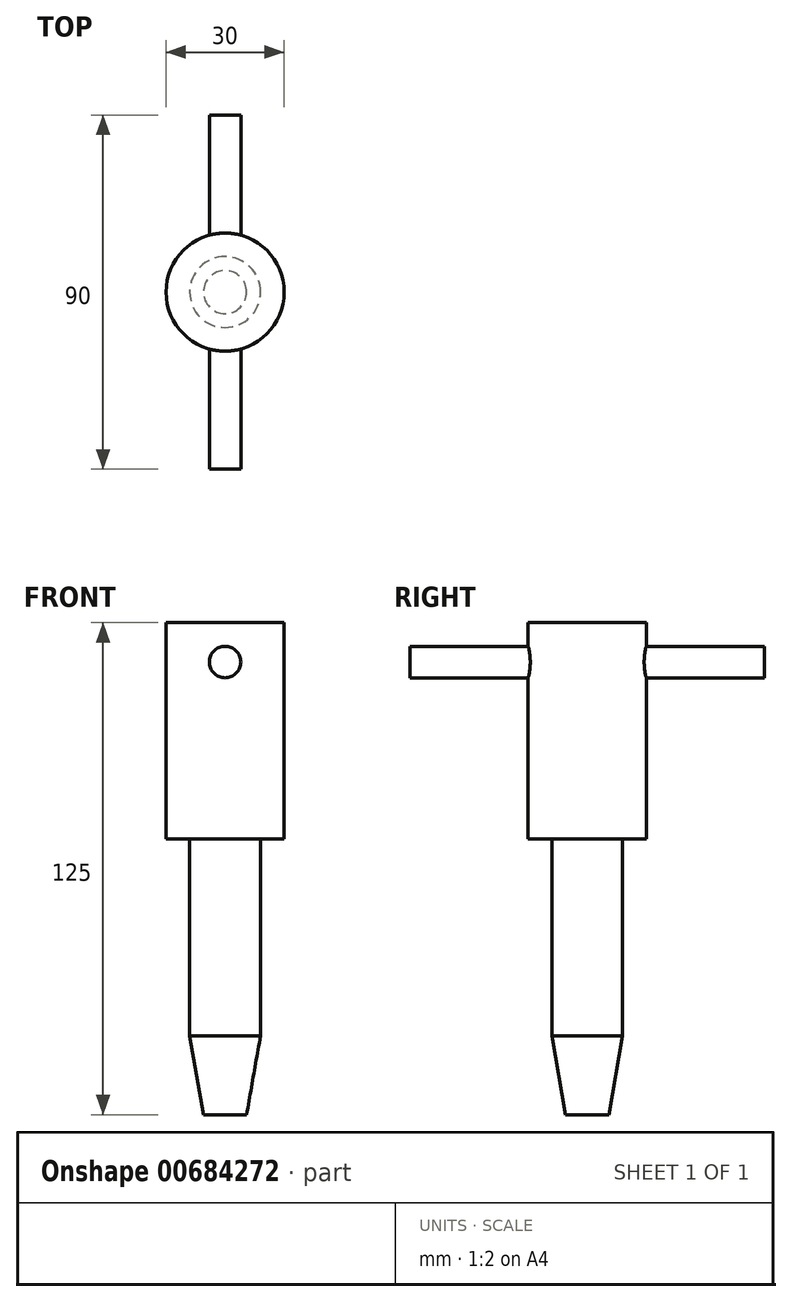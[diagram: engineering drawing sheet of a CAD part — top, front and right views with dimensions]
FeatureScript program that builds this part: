
annotation { "Feature Type Name" : "Feature", "Feature Type Description" : "" }
export const myFeature = defineFeature(function(context is Context, id is Id, definition is map)
    precondition{}
    {
        {
            var Q0;
            Q0=qCreatedBy(makeId("Front.planeOp"),FACE);
            var sketch = newSketch(context, id + "F0", { "sketchPlane" : qUnion([Q0])});
            skLineSegment(sketch, "E0", {"start": v(0, 0) * mm, "end": v(0, -70) * mm});
            skLineSegment(sketch, "E1", {"start": v(0, -70) * mm, "end": v(5.47, -70) * mm});
            skLineSegment(sketch, "E2", {"start": v(5.47, -70) * mm, "end": v(9, -50) * mm});
            skLineSegment(sketch, "E3", {"start": v(9, -50) * mm, "end": v(9, 0) * mm});
            skLineSegment(sketch, "E4", {"start": v(9, 0) * mm, "end": v(15, 0) * mm});
            skLineSegment(sketch, "E5", {"start": v(15, 0) * mm, "end": v(15, 55) * mm});
            skLineSegment(sketch, "E6", {"start": v(15, 55) * mm, "end": v(0, 55) * mm});
            skLineSegment(sketch, "E7", {"start": v(0, 55) * mm, "end": v(0, 0) * mm});
            skSolve(sketch);
        }
        {
            var Q0;
            Q0=makeQuery(id+"F0.imprint","IMPRINT",FACE,{"disambiguationData":[TD([[makeQuery(id+"F0.imprint","IMPRINT",EDGE,{"derivedFrom":sQuery(id+"F0.wireOp",EDGE,"E0")}),1.0]])]});
            var Q1;
            Q1=sQuery(id+"F0.wireOp",EDGE,"E7");
            revolve(context, id + "F1", {"entities" : qUnion([Q0]), "axis" : qUnion([Q1]), "revolveType" : RevolveType.FULL});
        }
        {
            var Q0;
            Q0=qCreatedBy(makeId("Front.planeOp"),FACE);
            var sketch = newSketch(context, id + "F2", { "sketchPlane" : qUnion([Q0])});
            skLineSegment(sketch, "E8.0", {"start": v(-15, 55) * mm, "end": v(15, 55) * mm});
            skLineSegment(sketch, "E9", {"start": v(0, 55) * mm, "end": v(0, 45) * mm});
            skCircle(sketch, "E10", {"center": v(0, 45) * mm, "radius": 4 * mm});
            skSolve(sketch);
        }
        {
            var Q0;
            Q0=qSketchRegion(id+"F2",true);
            extrude(context, id + "F3", {"entities" : qUnion([Q0]), "operationType" : NewBodyOperationType.ADD, "endBound" : BoundingType.SYMMETRIC, "depth" : 90 * mm, "offsetDistance" : 25 * mm});
        }
    });
